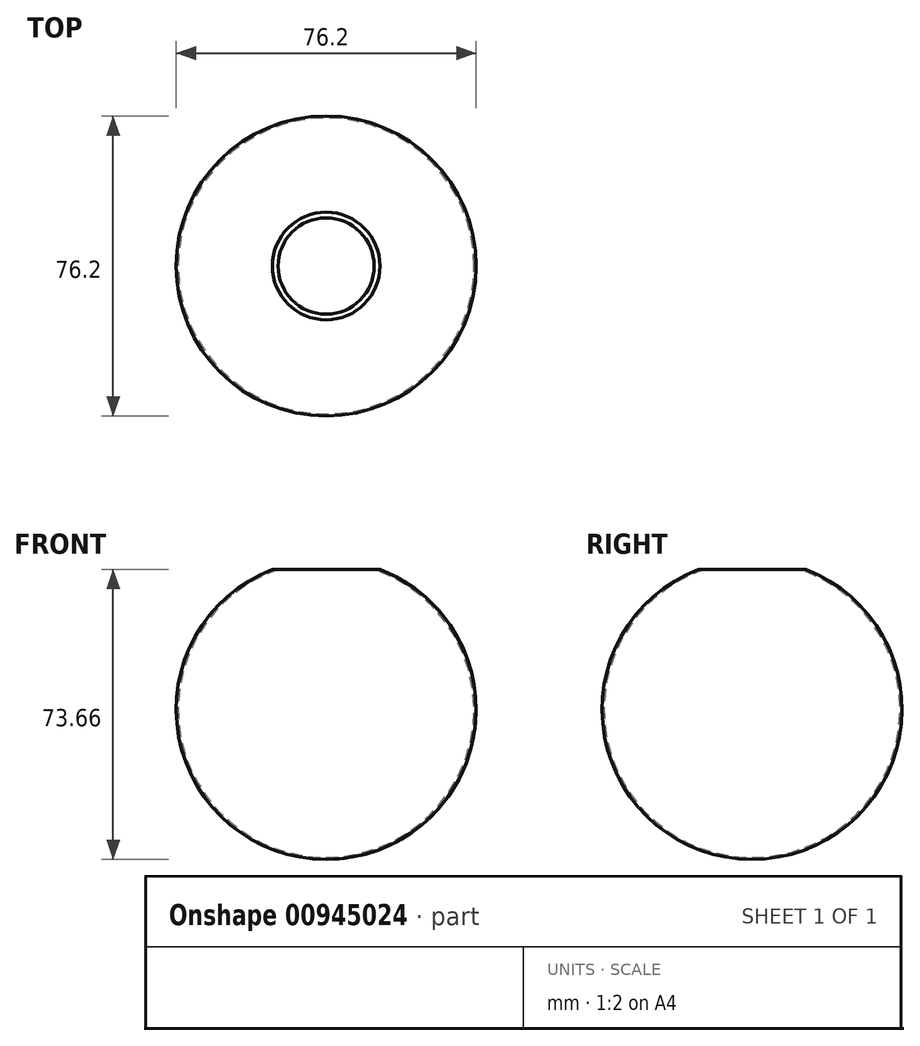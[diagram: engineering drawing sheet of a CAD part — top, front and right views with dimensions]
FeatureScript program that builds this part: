
annotation { "Feature Type Name" : "Feature", "Feature Type Description" : "" }
export const myFeature = defineFeature(function(context is Context, id is Id, definition is map)
    precondition{}
    {
        {
            var Q0;
            Q0=qCreatedBy(makeId("Front.planeOp"),FACE);
            var sketch = newSketch(context, id + "F0", { "sketchPlane" : qUnion([Q0])});
            skArc(sketch, "E0", {"start": v(0, -38.1) * mm, "mid": v(38.1, 0) * mm, "end": v(0, 38.1) * mm});
            skLineSegment(sketch, "E1", {"start": v(0, 38.1) * mm, "end": v(0, -38.1) * mm});
            skSolve(sketch);
        }
        {
            var Q0;
            Q0=makeQuery(id+"F0.imprint","IMPRINT",FACE,{"disambiguationData":[TD([[makeQuery(id+"F0.imprint","IMPRINT",EDGE,{"derivedFrom":sQuery(id+"F0.wireOp",EDGE,"E0")}),1.0]])]});
            var Q1;
            Q1=sQuery(id+"F0.wireOp",EDGE,"E1");
            revolve(context, id + "F1", {"surfaceOperationType" : NewSurfaceOperationType.NEW, "entities" : qUnion([Q0]), "axis" : qUnion([Q1]), "revolveType" : RevolveType.FULL});
        }
        {
            var Q0;
            Q0=qCreatedBy(makeId("Top.planeOp"),FACE);
            cPlane(context, id + "F2", {"entities" : qUnion([Q0]), "cplaneType" : CPlaneType.OFFSET, "offset" : 35.56 * mm, "width" : 152.4 * mm, "height" : 152.4 * mm});
        }
        {
            var Q0;
            Q0=qCreatedBy(id+"F2.planeOp",FACE);
            var sketch = newSketch(context, id + "F3", { "sketchPlane" : qUnion([Q0])});
            skLineSegment(sketch, "E2.bottom", {"start": v(16.51, -16.51) * mm, "end": v(-16.51, -16.51) * mm});
            skLineSegment(sketch, "E2.top", {"start": v(16.51, 16.51) * mm, "end": v(-16.51, 16.51) * mm});
            skLineSegment(sketch, "E2.left", {"start": v(16.51, -16.51) * mm, "end": v(16.51, 16.51) * mm});
            skLineSegment(sketch, "E2.right", {"start": v(-16.51, -16.51) * mm, "end": v(-16.51, 16.51) * mm});
            skPoint(sketch, "E2.middle", {"position": v(0, 0) * mm});
            skLineSegment(sketch, "E3", {"start": v(-16.51, -16.51) * mm, "end": v(16.51, -16.51) * mm});
            skSolve(sketch);
        }
        {
            var Q0;
            Q0 = qSketchRegion(id + "F3", true);
            extrude(context, id + "F4", {"entities" : qUnion([Q0]), "operationType" : NewBodyOperationType.REMOVE, "depth" : 25.4 * mm, "offsetDistance" : 25.4 * mm});
        }
        {
            var Q0;
            Q0=makeQuery(id+"F4.boolean.opBoolean","COPY",FACE,{"derivedFrom":makeQuery(id+"F4.opExtrude","CAP_FACE",FACE,{"disambiguationData":[OSD([sQuery(id+"F3.wireOp",EDGE,"E2.left"),sQuery(id+"F3.wireOp",EDGE,"E3"),sQuery(id+"F3.wireOp",EDGE,"E2.top"),sQuery(id+"F3.wireOp",EDGE,"E2.right")])],"isStart":true})});
            shell(context, id + "F5", {"entities" : qUnion([Q0]), "thickness" : 0.5 * mm});
        }
    });
